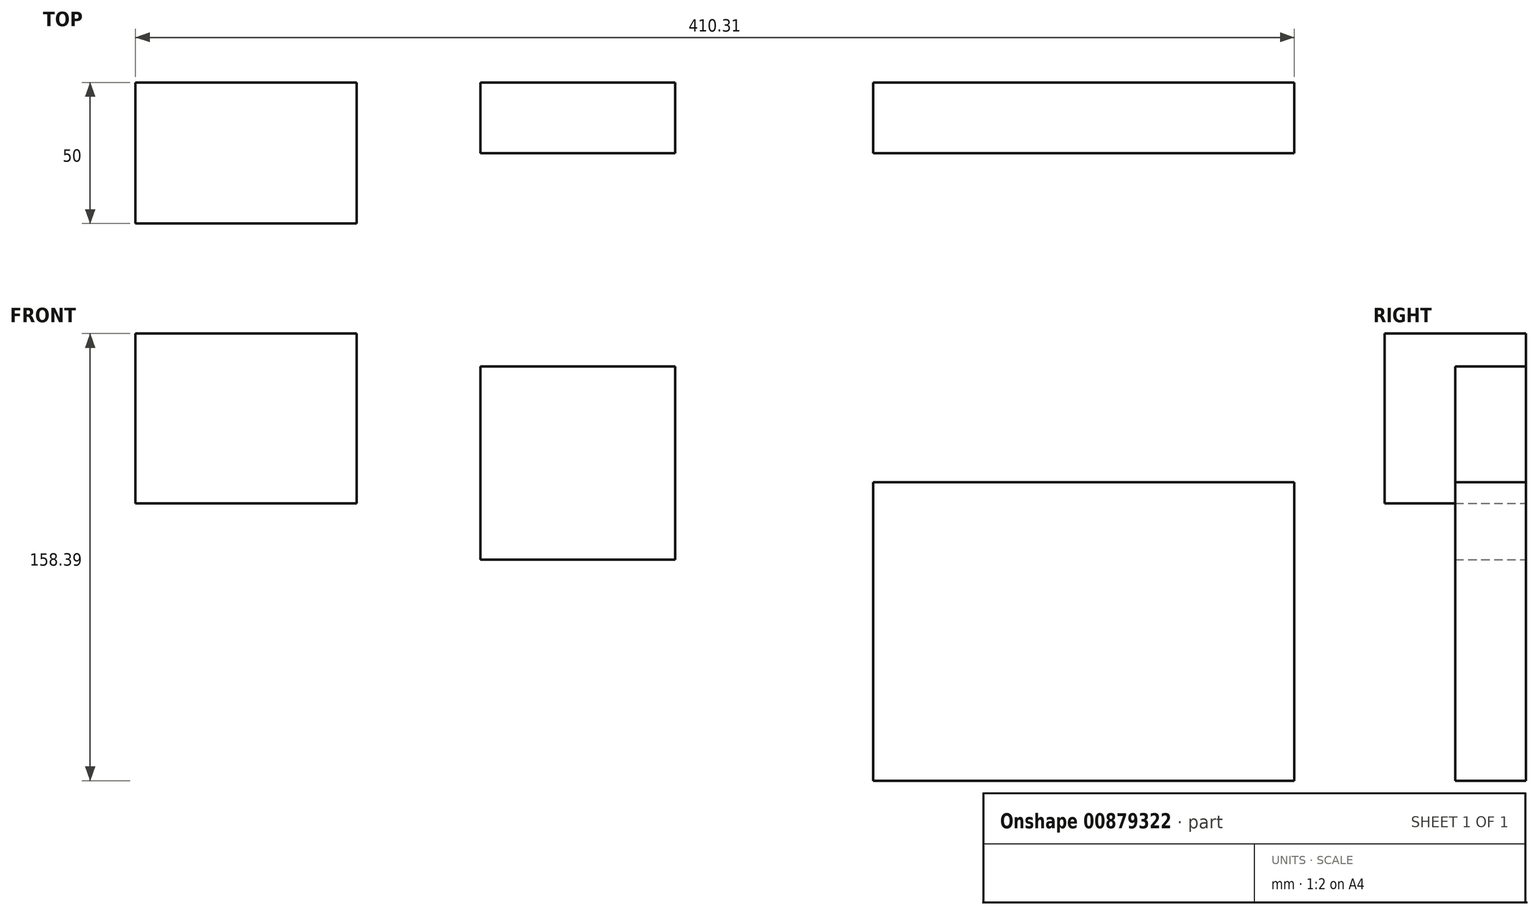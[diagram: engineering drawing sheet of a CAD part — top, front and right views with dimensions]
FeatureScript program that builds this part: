
annotation { "Feature Type Name" : "Feature", "Feature Type Description" : "" }
export const myFeature = defineFeature(function(context is Context, id is Id, definition is map)
    precondition{}
    {
        {
            var Q0;
            Q0=qCreatedBy(makeId("Front.planeOp"),FACE);
            var sketch = newSketch(context, id + "F0", { "sketchPlane" : qUnion([Q0])});
            skLineSegment(sketch, "E0.bottom", {"start": v(-377.87, 31.85) * mm, "end": v(-299.55, 31.85) * mm});
            skLineSegment(sketch, "E0.top", {"start": v(-377.87, -28.35) * mm, "end": v(-299.55, -28.35) * mm});
            skLineSegment(sketch, "E0.left", {"start": v(-377.87, 31.85) * mm, "end": v(-377.87, -28.35) * mm});
            skLineSegment(sketch, "E0.right", {"start": v(-299.55, 31.85) * mm, "end": v(-299.55, -28.35) * mm});
            skLineSegment(sketch, "E1.bottom", {"start": v(-255.71, 20.16) * mm, "end": v(-186.74, 20.16) * mm});
            skLineSegment(sketch, "E1.top", {"start": v(-255.71, -48.22) * mm, "end": v(-186.74, -48.22) * mm});
            skLineSegment(sketch, "E1.left", {"start": v(-255.71, 20.16) * mm, "end": v(-255.71, -48.22) * mm});
            skLineSegment(sketch, "E1.right", {"start": v(-186.74, 20.16) * mm, "end": v(-186.74, -48.22) * mm});
            skLineSegment(sketch, "E2.bottom", {"start": v(-116.6, -20.75) * mm, "end": v(32.44, -20.75) * mm});
            skLineSegment(sketch, "E2.top", {"start": v(-116.6, -126.54) * mm, "end": v(32.44, -126.54) * mm});
            skLineSegment(sketch, "E2.left", {"start": v(-116.6, -20.75) * mm, "end": v(-116.6, -126.54) * mm});
            skLineSegment(sketch, "E2.right", {"start": v(32.44, -20.75) * mm, "end": v(32.44, -126.54) * mm});
            skSolve(sketch);
        }
        {
            var Q0;
            Q0 = qSketchRegion(id + "F0", true);
            extrude(context, id + "F1", {"entities" : qUnion([Q0]), "depth" : 25 * mm, "offsetDistance" : 25 * mm});
        }
        {
            var Q0;
            Q0=makeQuery(id+"F1.opExtrude","CAP_FACE",FACE,{"disambiguationData":[OSD([sQuery(id+"F0.wireOp",EDGE,"E0.bottom"),sQuery(id+"F0.wireOp",EDGE,"E0.top"),sQuery(id+"F0.wireOp",EDGE,"E0.left"),sQuery(id+"F0.wireOp",EDGE,"E0.right")])],"isStart":false});
            extrude(context, id + "F2", {"entities" : qUnion([Q0]), "operationType" : NewBodyOperationType.ADD, "depth" : 25 * mm, "offsetDistance" : 25 * mm});
        }
    });
